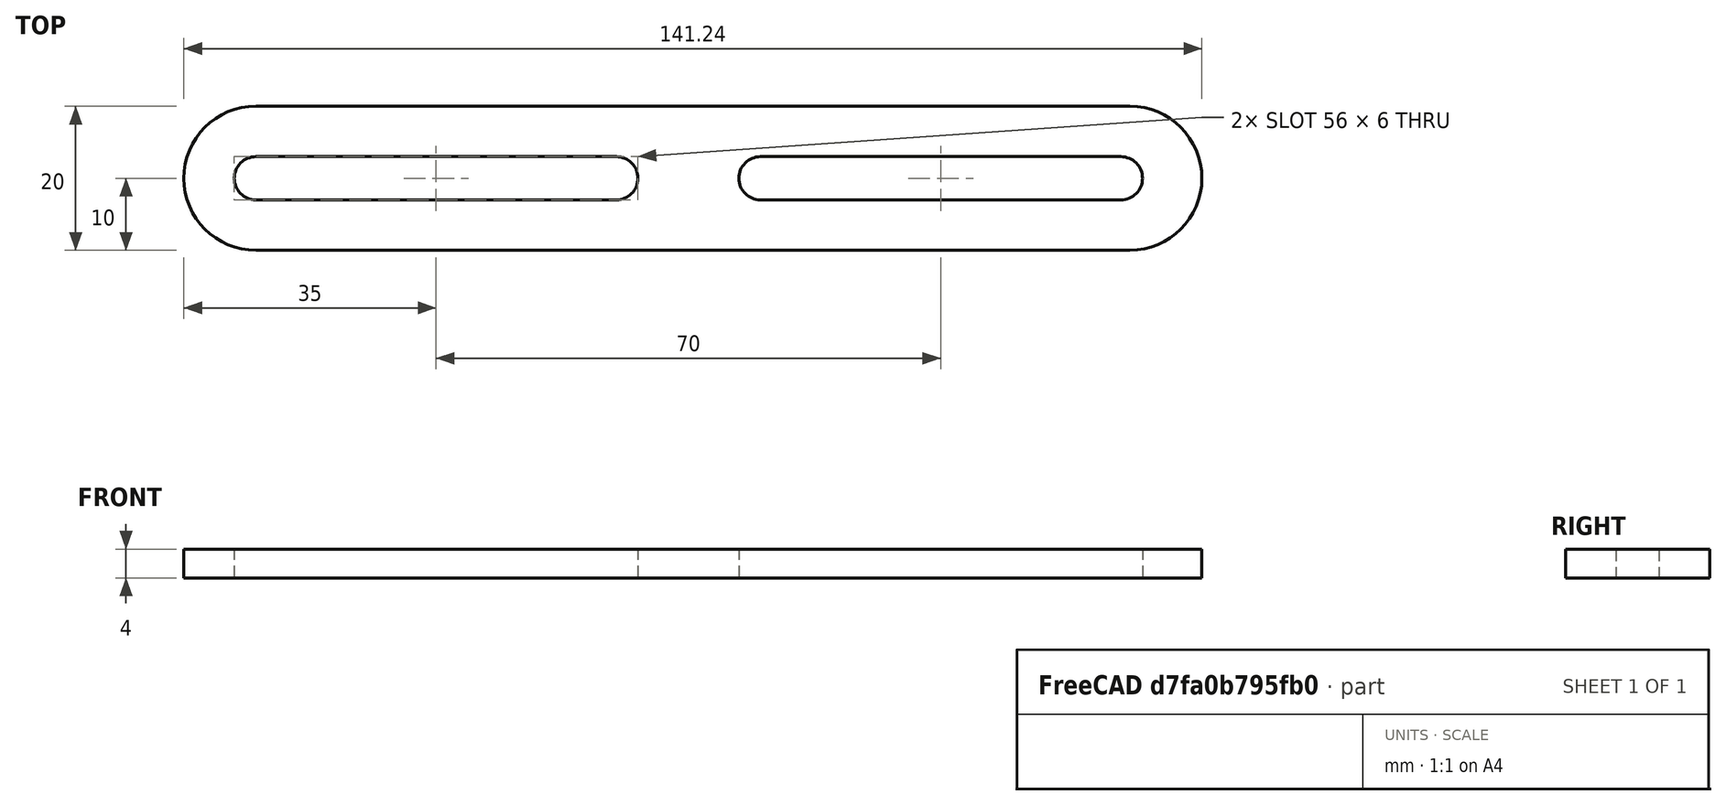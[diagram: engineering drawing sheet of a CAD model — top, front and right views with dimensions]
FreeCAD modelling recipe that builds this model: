
FCSTD DOCUMENT  (FreeCAD 0.19R24276 (Git))
Label: Spring_holder
License: All rights reserved
LicenseURL: http://en.wikipedia.org/wiki/All_rights_reserved
objects: Sketcher::SketchObject×1, PartDesign::Pad×1, PartDesign::Body×1
note: 4 computed .brp shape members not serialized (recipe doc carries the construction recipe); baked Part::Feature solids carry a one-line shape summary decoded from their .brp

FEATURE [Sketcher::SketchObject] Sketch
  FullyConstrained = false
  MapMode = 5
  Support = -> [XY_Plane]
  sketch-geometry (12):
    g0: ArcOfCircle CenterX=0 CenterY=0 CenterZ=0 NormalX=0 NormalY=0 NormalZ=1 AngleXU=0 Radius=3 StartAngle=1.5708 EndAngle=4.71239
    g1: ArcOfCircle CenterX=50 CenterY=1e-16 CenterZ=0 NormalX=0 NormalY=0 NormalZ=1 AngleXU=0 Radius=3 StartAngle=4.71239 EndAngle=7.85398
    g2: LineSegment StartX=0 StartY=-3 StartZ=0 EndX=50 EndY=-3 EndZ=0
    g3: LineSegment StartX=-4e-16 StartY=3 StartZ=0 EndX=50 EndY=3 EndZ=0
    g4: ArcOfCircle CenterX=70 CenterY=0 CenterZ=0 NormalX=0 NormalY=0 NormalZ=1 AngleXU=0 Radius=3 StartAngle=1.5708 EndAngle=4.71239
    g5: ArcOfCircle CenterX=120 CenterY=-1e-16 CenterZ=0 NormalX=0 NormalY=0 NormalZ=1 AngleXU=0 Radius=3 StartAngle=4.71239 EndAngle=7.85398
    g6: LineSegment StartX=70 StartY=-3 StartZ=0 EndX=120 EndY=-3 EndZ=0
    g7: LineSegment StartX=70 StartY=3 StartZ=0 EndX=120 EndY=3 EndZ=0
    g8: ArcOfCircle CenterX=0 CenterY=0 CenterZ=0 NormalX=0 NormalY=0 NormalZ=1 AngleXU=0 Radius=10 StartAngle=1.5708 EndAngle=4.71239
    g9: ArcOfCircle CenterX=121.238 CenterY=0 CenterZ=0 NormalX=0 NormalY=0 NormalZ=1 AngleXU=0 Radius=10 StartAngle=4.71239 EndAngle=7.85398
    g10: LineSegment StartX=0 StartY=-10 StartZ=0 EndX=121.238 EndY=-10 EndZ=0
    g11: LineSegment StartX=-1.6e-15 StartY=10 StartZ=0 EndX=121.238 EndY=10 EndZ=0
  constraints (27):
    c: Tangent(g0,g3) = 1.5708
    c: Tangent(g0,g2) = -1.5708
    c: Tangent(g2,g1) = -1.5708
    c: Tangent(g3,g1) = 1.5708
    c: Horizontal(g2)
    c: Equal(g0,g1)
    c: Coincident(g0,g-1)
    c: Diameter(g0) = 6
    c: DistanceX(g0,g1) = 50
    c: Tangent(g4,g7) = 1.5708
    c: Tangent(g4,g6) = -1.5708
    c: Tangent(g6,g5) = -1.5708
    c: Tangent(g7,g5) = 1.5708
    c: Horizontal(g6)
    c: Equal(g4,g5)
    c: PointOnObject(g4,g-1)
    c: Diameter(g4) = 6
    c: DistanceX(g4,g5) = 50
    c: DistanceX(g0,g5) = 120
    c: Tangent(g8,g11) = 1.5708
    c: Tangent(g8,g10) = -1.5708
    c: Tangent(g10,g9) = -1.5708
    c: Tangent(g11,g9) = 1.5708
    c: Horizontal(g10)
    c: Equal(g8,g9)
    c: Coincident(g8,g0)
    c: Diameter(g9) = 20
FEATURE [PartDesign::Pad] Pad
  Direction = (1,1,1)
  Length = 4
  Length2 = 100
  Profile = -> Sketch
  Type = 0
FEATURE [PartDesign::Body] Body
  Group = -> [Sketch,Pad]
  Origin = -> Origin
  Tip = -> Pad
